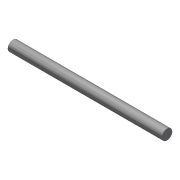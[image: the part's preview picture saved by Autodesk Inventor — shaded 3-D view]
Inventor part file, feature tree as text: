
AUTODESK INVENTOR PART (.ipt)
format: ipt  version: 2016 (Build 200138000, 138)  size: 69,120 bytes
history: native  units: in
note: dims shown in document units (in); Inventor stores cm internally (conversion verified against a paired STEP export)
features: extrude x1, sketch x1
ambient origin geometry x8: Origin, YZ Plane, XZ Plane, XY Plane, X Axis, Y Axis, Z Axis, Center Point
bodies: Solid1 (feature_tree)
feature tree (2):
  extrude  "Extrusion1"  Depth=5.5625in TaperAngle=0.0deg
  sketch  "Sketch1"  dims[d0=0.375in d1=5.5625in d2=0.0in]
